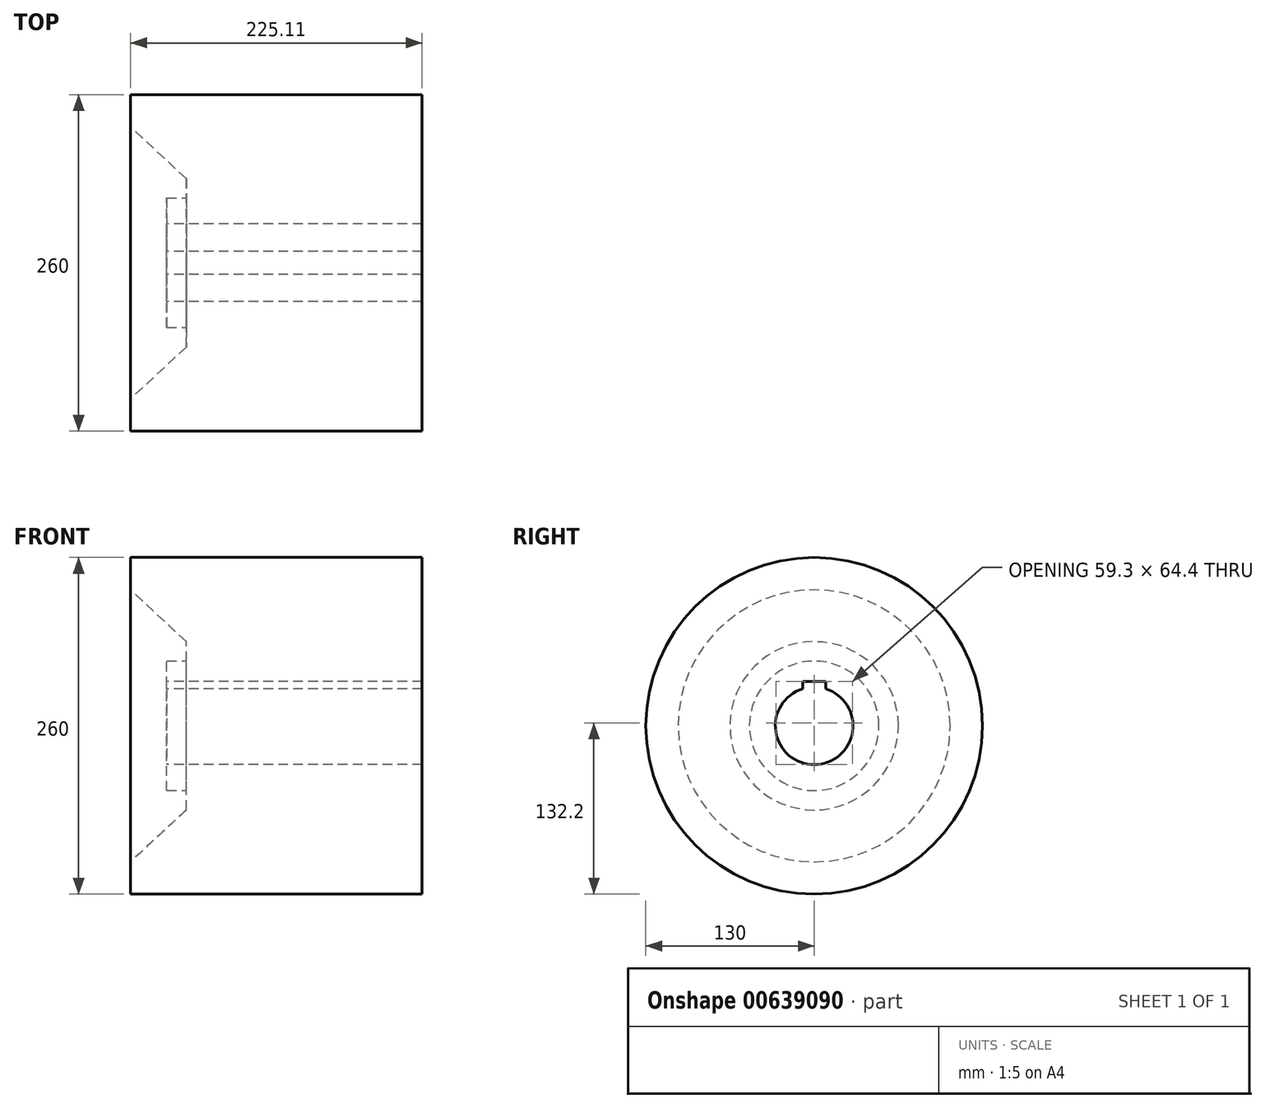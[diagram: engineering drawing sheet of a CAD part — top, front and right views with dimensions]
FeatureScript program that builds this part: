
annotation { "Feature Type Name" : "Feature", "Feature Type Description" : "" }
export const myFeature = defineFeature(function(context is Context, id is Id, definition is map)
    precondition{}
    {
        {
            var Q0;
            Q0=qCreatedBy(makeId("Front.planeOp"),FACE);
            var sketch = newSketch(context, id + "F0", { "sketchPlane" : qUnion([Q0])});
            skLineSegment(sketch, "E0", {"start": v(-113.2, 0) * mm, "end": v(290.03, 0) * mm, "construction": true});
            skLineSegment(sketch, "E1.bottom", {"start": v(0, 0) * mm, "end": v(225.1, 0) * mm});
            skLineSegment(sketch, "E1.top", {"start": v(0, -130) * mm, "end": v(225.1, -130) * mm});
            skLineSegment(sketch, "E1.left", {"start": v(0, 0) * mm, "end": v(0, -130) * mm});
            skLineSegment(sketch, "E1.right", {"start": v(225.1, 0) * mm, "end": v(225.1, -130) * mm});
            skLineSegment(sketch, "E2.bottom", {"start": v(0, 0) * mm, "end": v(28, 0) * mm});
            skSolve(sketch);
        }
        {
            var Q0;
            Q0=makeQuery(id+"F0.imprint","IMPRINT",FACE,{"disambiguationData":[TD([[makeQuery(id+"F0.imprint","IMPRINT",EDGE,{"derivedFrom":sQuery(id+"F0.wireOp",EDGE,"E1.bottom")}),-1.0]])]});
            var Q1;
            Q1=sQuery(id+"F0.wireOp",EDGE,"E0");
            revolve(context, id + "F1", {"entities" : qUnion([Q0]), "axis" : qUnion([Q1]), "revolveType" : RevolveType.FULL});
        }
        {
            var Q0;
            Q0=qCreatedBy(makeId("Front.planeOp"),FACE);
            var sketch = newSketch(context, id + "F2", { "sketchPlane" : qUnion([Q0])});
            skLineSegment(sketch, "E3", {"start": v(0, 0) * mm, "end": v(0, -105) * mm});
            skLineSegment(sketch, "E4", {"start": v(0, 0) * mm, "end": v(28, 0) * mm});
            skLineSegment(sketch, "E5", {"start": v(28, 0) * mm, "end": v(28, -50) * mm});
            skLineSegment(sketch, "E6", {"start": v(28, -50) * mm, "end": v(43, -50) * mm});
            skLineSegment(sketch, "E7", {"start": v(43, -50) * mm, "end": v(43, -65) * mm});
            skLineSegment(sketch, "E8", {"start": v(43, -65) * mm, "end": v(0, -105) * mm});
            skSolve(sketch);
        }
        {
            var Q0;
            Q0 = qSketchRegion(id + "F2", true);
            var Q1;
            Q1=sQuery(id+"F0.wireOp",EDGE,"E0");
            revolve(context, id + "F3", {"operationType" : NewBodyOperationType.REMOVE, "entities" : qUnion([Q0]), "axis" : qUnion([Q1]), "revolveType" : RevolveType.FULL, "oppositeDirection" : true});
        }
        {
            var Q0;
            Q0=qCreatedBy(makeId("Right.planeOp"),FACE);
            var sketch = newSketch(context, id + "F4", { "sketchPlane" : qUnion([Q0])});
            skCircle(sketch, "E9", {"center": v(0, 0) * mm, "radius": 30 * mm});
            skLineSegment(sketch, "E10", {"start": v(0, 34.4) * mm, "end": v(-9, 34.4) * mm});
            skLineSegment(sketch, "E11", {"start": v(0, 34.4) * mm, "end": v(0, -30) * mm});
            skLineSegment(sketch, "E12", {"start": v(0, 34.4) * mm, "end": v(9, 34.4) * mm});
            skLineSegment(sketch, "E13", {"start": v(9, 34.4) * mm, "end": v(9, 24.4) * mm});
            skLineSegment(sketch, "E14", {"start": v(9, 24.4) * mm, "end": v(-9, 24.4) * mm});
            skLineSegment(sketch, "E15", {"start": v(-9, 24.4) * mm, "end": v(-9, 34.4) * mm});
            skSolve(sketch);
        }
        {
            var Q0;
            Q0=makeQuery(id+"F4.imprint","IMPRINT",FACE,{"disambiguationData":[TD([[makeQuery(id+"F4.imprint","IMPRINT",EDGE,{"derivedFrom":sQuery(id+"F4.wireOp",EDGE,"E9")}),1.0]])]});
            var Q1;
            {var subQ5=sQuery(id+"F4.wireOp",EDGE,"E10");Q1=makeQuery(id+"F4.imprint","IMPRINT",FACE,{"disambiguationData":[TD([[makeQuery(id+"F4.imprint","IMPRINT",EDGE,{"derivedFrom":subQ5}),1.0]])]});}
            var Q2;
            {var subQ5=sQuery(id+"F4.wireOp",EDGE,"E12");Q2=makeQuery(id+"F4.imprint","IMPRINT",FACE,{"disambiguationData":[TD([[makeQuery(id+"F4.imprint","IMPRINT",EDGE,{"derivedFrom":subQ5}),-1.0]])]});}
            extrude(context, id + "F5", {"entities" : qUnion([Q0, Q1, Q2]), "operationType" : NewBodyOperationType.REMOVE, "endBound" : BoundingType.THROUGH_ALL, "depth" : 25 * mm, "offsetDistance" : 25 * mm});
        }
    });
